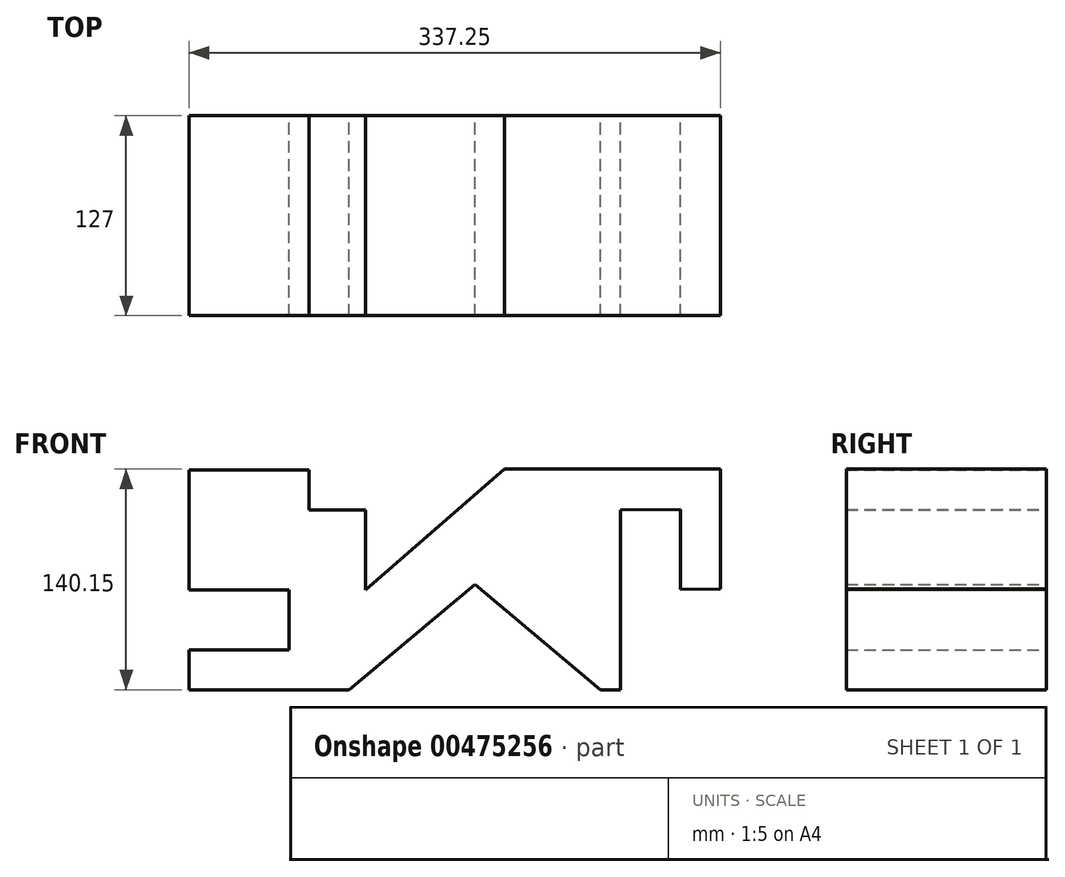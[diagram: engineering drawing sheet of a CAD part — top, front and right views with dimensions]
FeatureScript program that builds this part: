
annotation { "Feature Type Name" : "Feature", "Feature Type Description" : "" }
export const myFeature = defineFeature(function(context is Context, id is Id, definition is map)
    precondition{}
    {
        {
            var Q0;
            Q0=qCreatedBy(makeId("Front.planeOp"),FACE);
            var sketch = newSketch(context, id + "F0", { "sketchPlane" : qUnion([Q0])});
            skLineSegment(sketch, "E0", {"start": v(-104.97, 114.3) * mm, "end": v(-104.97, 38.1) * mm});
            skLineSegment(sketch, "E1", {"start": v(-104.97, 38.1) * mm, "end": v(-41.47, 38.1) * mm});
            skLineSegment(sketch, "E2", {"start": v(-41.47, 38.1) * mm, "end": v(-41.47, 0) * mm});
            skLineSegment(sketch, "E3", {"start": v(-41.47, 0) * mm, "end": v(-104.97, 0) * mm});
            skLineSegment(sketch, "E4", {"start": v(-104.97, 0) * mm, "end": v(-104.97, -25.4) * mm});
            skLineSegment(sketch, "E5", {"start": v(-104.97, -25.4) * mm, "end": v(-3.37, -25.4) * mm});
            skLineSegment(sketch, "E6", {"start": v(-3.37, -25.4) * mm, "end": v(76.45, 41.57) * mm});
            skLineSegment(sketch, "E7", {"start": v(76.45, 41.57) * mm, "end": v(156.26, -25.4) * mm});
            skLineSegment(sketch, "E8", {"start": v(156.26, -25.4) * mm, "end": v(168.96, -25.4) * mm});
            skLineSegment(sketch, "E9", {"start": v(168.78, -25.4) * mm, "end": v(168.78, 88.9) * mm});
            skLineSegment(sketch, "E10", {"start": v(168.78, 88.9) * mm, "end": v(206.88, 89.17) * mm});
            skLineSegment(sketch, "E11", {"start": v(206.88, 89.17) * mm, "end": v(206.88, 38.37) * mm});
            skLineSegment(sketch, "E12", {"start": v(206.88, 38.37) * mm, "end": v(232.28, 38.55) * mm});
            skLineSegment(sketch, "E13", {"start": v(232.28, 38.55) * mm, "end": v(232.28, 114.75) * mm});
            skLineSegment(sketch, "E14", {"start": v(232.28, 114.75) * mm, "end": v(95.12, 114.75) * mm});
            skLineSegment(sketch, "E15", {"start": v(95.12, 114.75) * mm, "end": v(6.94, 38.1) * mm});
            skLineSegment(sketch, "E16", {"start": v(6.94, 38.1) * mm, "end": v(6.94, 88.9) * mm});
            skLineSegment(sketch, "E17", {"start": v(6.94, 88.9) * mm, "end": v(-28.77, 88.9) * mm});
            skLineSegment(sketch, "E18", {"start": v(-28.77, 88.9) * mm, "end": v(-28.77, 114.3) * mm});
            skLineSegment(sketch, "E19", {"start": v(-28.77, 114.3) * mm, "end": v(-104.97, 114.3) * mm});
            skSolve(sketch);
        }
        {
            var Q0;
            Q0=makeQuery(id+"F0.imprint","IMPRINT",FACE,{"disambiguationData":[TD([[makeQuery(id+"F0.imprint","IMPRINT",EDGE,{"derivedFrom":sQuery(id+"F0.wireOp",EDGE,"E0")}),1.0]])]});
            extrude(context, id + "F1", {"entities" : qUnion([Q0]), "depth" : 127 * mm});
        }
    });
